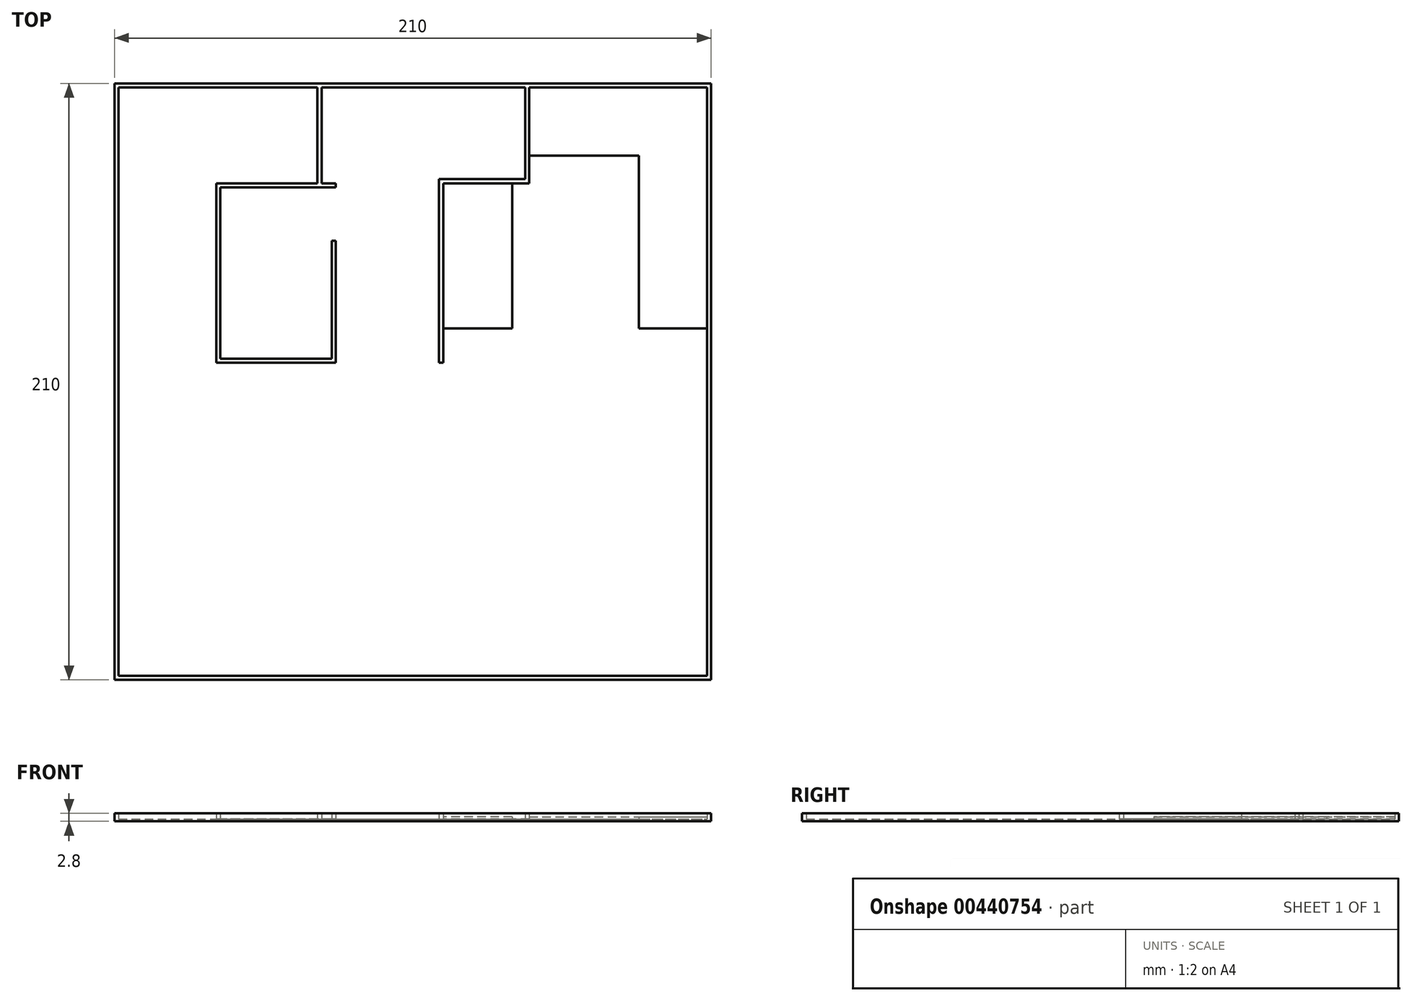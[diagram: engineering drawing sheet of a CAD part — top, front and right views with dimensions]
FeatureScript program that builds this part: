
annotation { "Feature Type Name" : "Feature", "Feature Type Description" : "" }
export const myFeature = defineFeature(function(context is Context, id is Id, definition is map)
    precondition{}
    {
        {
            var Q0;
            Q0=qCreatedBy(makeId("Top.planeOp"),FACE);
            var sketch = newSketch(context, id + "F0", { "sketchPlane" : qUnion([Q0])});
            skLineSegment(sketch, "E0.bottom", {"start": v(0, 0) * mm, "end": v(210, 0) * mm});
            skLineSegment(sketch, "E0.top", {"start": v(0, 210) * mm, "end": v(210, 210) * mm});
            skLineSegment(sketch, "E0.left", {"start": v(0, 0) * mm, "end": v(0, 210) * mm});
            skLineSegment(sketch, "E0.right", {"start": v(210, 0) * mm, "end": v(210, 210) * mm});
            skSolve(sketch);
        }
        {
            var Q0;
            Q0=makeQuery(id+"F0.imprint","IMPRINT",FACE,{"disambiguationData":[TD([[makeQuery(id+"F0.imprint","IMPRINT",EDGE,{"derivedFrom":sQuery(id+"F0.wireOp",EDGE,"E0.bottom")}),1.0]])]});
            extrude(context, id + "F1", {"entities" : qUnion([Q0]), "depth" : .8 * mm});
        }
        {
            var Q0;
            Q0=makeQuery(id+"F1.opExtrude","CAP_FACE",FACE,{"disambiguationData":[OSD([sQuery(id+"F0.wireOp",EDGE,"E0.bottom"),sQuery(id+"F0.wireOp",EDGE,"E0.top"),sQuery(id+"F0.wireOp",EDGE,"E0.left"),sQuery(id+"F0.wireOp",EDGE,"E0.right")])],"isStart":false});
            var sketch = newSketch(context, id + "F2", { "sketchPlane" : qUnion([Q0])});
            skLineSegment(sketch, "E1.0", {"start": v(1.44, 1.44) * mm, "end": v(208.56, 1.44) * mm});
            skLineSegment(sketch, "E1.1", {"start": v(1.44, 1.44) * mm, "end": v(1.44, 208.56) * mm});
            skLineSegment(sketch, "E1.2", {"start": v(1.44, 208.56) * mm, "end": v(208.56, 208.56) * mm});
            skLineSegment(sketch, "E1.3", {"start": v(208.56, 1.44) * mm, "end": v(208.56, 208.56) * mm});
            skLineSegment(sketch, "E2.0", {"start": v(0, 0) * mm, "end": v(210, 0) * mm});
            skLineSegment(sketch, "E3.0", {"start": v(0, 0) * mm, "end": v(0, 210) * mm});
            skLineSegment(sketch, "E4.0", {"start": v(0, 210) * mm, "end": v(210, 210) * mm});
            skLineSegment(sketch, "E5.0", {"start": v(210, 0) * mm, "end": v(210, 210) * mm});
            skSolve(sketch);
        }
        {
            var Q0;
            Q0=qSketchRegion(id+"F2",true);
            extrude(context, id + "F3", {"entities" : qUnion([Q0]), "operationType" : NewBodyOperationType.ADD, "depth" : 2 * mm});
        }
        {
            var Q0;
            Q0=makeQuery(id+"F1.opExtrude","CAP_FACE",FACE,{"disambiguationData":[OSD([sQuery(id+"F0.wireOp",EDGE,"E0.bottom"),sQuery(id+"F0.wireOp",EDGE,"E0.top"),sQuery(id+"F0.wireOp",EDGE,"E0.left"),sQuery(id+"F0.wireOp",EDGE,"E0.right")])],"isStart":false});
            var sketch = newSketch(context, id + "F4", { "sketchPlane" : qUnion([Q0])});
            skLineSegment(sketch, "E6", {"start": v(145.96, 208.56) * mm, "end": v(145.96, 174.81) * mm});
            skLineSegment(sketch, "E7", {"start": v(145.96, 174.81) * mm, "end": v(115.68, 174.81) * mm});
            skLineSegment(sketch, "E8", {"start": v(115.68, 174.81) * mm, "end": v(115.68, 111.64) * mm});
            skLineSegment(sketch, "E9", {"start": v(114.24, 111.64) * mm, "end": v(115.68, 111.64) * mm});
            skLineSegment(sketch, "E10", {"start": v(114.24, 111.64) * mm, "end": v(114.24, 176.25) * mm});
            skLineSegment(sketch, "E11", {"start": v(114.24, 176.25) * mm, "end": v(144.52, 176.25) * mm});
            skLineSegment(sketch, "E12", {"start": v(144.52, 208.56) * mm, "end": v(145.96, 208.56) * mm});
            skLineSegment(sketch, "E13", {"start": v(144.52, 208.56) * mm, "end": v(144.52, 176.25) * mm});
            skLineSegment(sketch, "E14", {"start": v(72.89, 208.56) * mm, "end": v(72.89, 174.81) * mm});
            skLineSegment(sketch, "E15", {"start": v(77.89, 174.81) * mm, "end": v(72.89, 174.81) * mm});
            skLineSegment(sketch, "E16", {"start": v(35.77, 174.81) * mm, "end": v(35.77, 111.64) * mm});
            skLineSegment(sketch, "E17", {"start": v(35.77, 111.64) * mm, "end": v(77.89, 111.64) * mm});
            skLineSegment(sketch, "E18", {"start": v(77.89, 111.64) * mm, "end": v(77.89, 154.6) * mm});
            skLineSegment(sketch, "E19", {"start": v(77.89, 154.6) * mm, "end": v(76.45, 154.6) * mm});
            skLineSegment(sketch, "E20", {"start": v(76.45, 154.6) * mm, "end": v(76.45, 113.08) * mm});
            skLineSegment(sketch, "E21", {"start": v(76.45, 113.08) * mm, "end": v(37.2, 113.08) * mm});
            skLineSegment(sketch, "E22", {"start": v(37.2, 113.08) * mm, "end": v(37.2, 173.37) * mm});
            skLineSegment(sketch, "E23", {"start": v(37.2, 173.37) * mm, "end": v(77.89, 173.37) * mm});
            skLineSegment(sketch, "E24", {"start": v(77.89, 173.37) * mm, "end": v(77.89, 174.81) * mm});
            skLineSegment(sketch, "E25", {"start": v(71.45, 208.56) * mm, "end": v(72.89, 208.56) * mm});
            skLineSegment(sketch, "E26", {"start": v(71.45, 208.56) * mm, "end": v(71.45, 174.81) * mm});
            skPoint(sketch, "E27.end.orphan", {"position": v(77.89, 179.23) * mm});
            skLineSegment(sketch, "E28.trimOffspring", {"start": v(71.45, 174.81) * mm, "end": v(35.77, 174.81) * mm});
            skSolve(sketch);
        }
        {
            var Q0;
            Q0 = qSketchRegion(id + "F4", true);
            var Q1;
            Q1=makeQuery(id+"F3.opExtrude","CAP_FACE",FACE,{"disambiguationData":[OSD([sQuery(id+"F2.wireOp",EDGE,"E1.0"),sQuery(id+"F2.wireOp",EDGE,"E1.1"),sQuery(id+"F2.wireOp",EDGE,"E1.2"),sQuery(id+"F2.wireOp",EDGE,"E1.3"),sQuery(id+"F2.wireOp",EDGE,"E2.0"),sQuery(id+"F2.wireOp",EDGE,"E3.0"),sQuery(id+"F2.wireOp",EDGE,"E4.0"),sQuery(id+"F2.wireOp",EDGE,"E5.0")])],"isStart":false});
            extrude(context, id + "F5", {"entities" : qUnion([Q0]), "operationType" : NewBodyOperationType.ADD, "endBound" : BoundingType.UP_TO_SURFACE, "endBoundEntityFace" : qUnion([Q1]), "depth" : 25 * mm});
        }
        {
            var Q0;
            Q0=makeQuery(id+"F1.opExtrude","CAP_FACE",FACE,{"disambiguationData":[OSD([sQuery(id+"F0.wireOp",EDGE,"E0.bottom"),sQuery(id+"F0.wireOp",EDGE,"E0.top"),sQuery(id+"F0.wireOp",EDGE,"E0.left"),sQuery(id+"F0.wireOp",EDGE,"E0.right")])],"isStart":false});
            var sketch = newSketch(context, id + "F6", { "sketchPlane" : qUnion([Q0])});
            skLineSegment(sketch, "E29", {"start": v(145.96, 208.56) * mm, "end": v(145.96, 184.56) * mm});
            skLineSegment(sketch, "E30", {"start": v(145.96, 184.56) * mm, "end": v(184.56, 184.56) * mm});
            skLineSegment(sketch, "E31", {"start": v(184.56, 184.56) * mm, "end": v(184.56, 123.75) * mm});
            skLineSegment(sketch, "E32", {"start": v(184.56, 123.75) * mm, "end": v(208.56, 123.75) * mm});
            skLineSegment(sketch, "E33", {"start": v(208.56, 123.75) * mm, "end": v(208.56, 208.56) * mm});
            skLineSegment(sketch, "E34", {"start": v(208.56, 208.56) * mm, "end": v(145.96, 208.56) * mm});
            skLineSegment(sketch, "E35", {"start": v(145.96, 184.56) * mm, "end": v(145.96, 208.56) * mm});
            skLineSegment(sketch, "E36", {"start": v(139.9, 174.81) * mm, "end": v(139.9, 123.75) * mm});
            skLineSegment(sketch, "E37", {"start": v(139.9, 123.75) * mm, "end": v(115.68, 123.75) * mm});
            skLineSegment(sketch, "E38", {"start": v(115.68, 123.75) * mm, "end": v(115.68, 174.81) * mm});
            skLineSegment(sketch, "E39", {"start": v(115.68, 174.81) * mm, "end": v(139.9, 174.81) * mm});
            skSolve(sketch);
        }
        {
            var Q0;
            Q0 = qSketchRegion(id + "F6", true);
            extrude(context, id + "F7", {"entities" : qUnion([Q0]), "operationType" : NewBodyOperationType.ADD, "depth" : .8 * mm});
        }
    });
